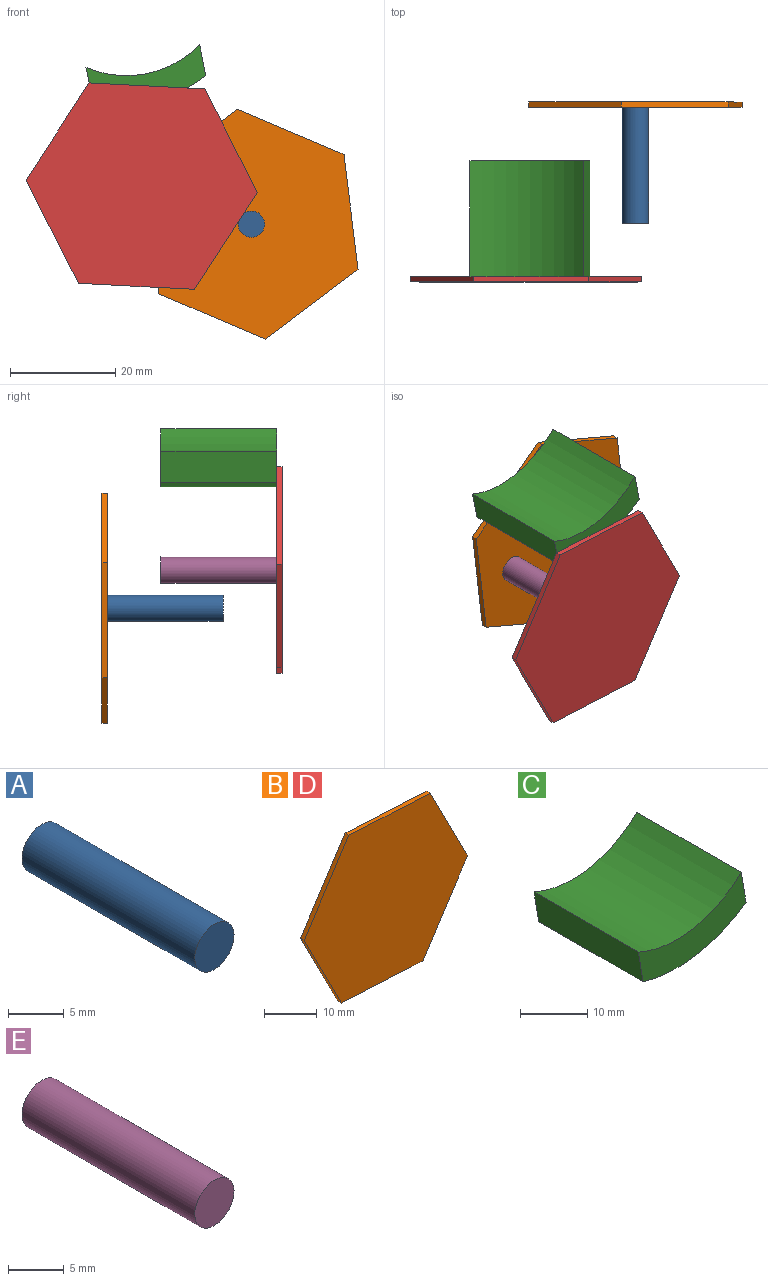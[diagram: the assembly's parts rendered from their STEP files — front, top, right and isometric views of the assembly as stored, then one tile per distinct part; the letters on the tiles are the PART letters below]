
ASSEMBLY  parts=5 mates=3
PART A: 3 faces, bbox 5x22x5 mm
  f0: cylinder r=2.5mm len=22mm, axis (0,1,0), area 345.6mm2, adj f1,f2
  f1: plane 5x5mm, normal (0,-1,0), area 19.6mm2, adj f0
  f2: plane 5x5mm, normal (0,1,0), area 19.6mm2, adj f0
PART B: 8 faces, bbox 43.9x1x39.2 mm
  f0: plane 18.46x11.98mm, normal (0.84,0,-0.54), area 22mm2, adj f1,f5,f6,f7
  f1: plane 19.6x10mm, normal (0.89,0,0.45), area 22mm2, adj f0,f2,f6,f7
  f2: plane 21.97x1.14mm, normal (0.05,0,1), area 22mm2, adj f1,f3,f6,f7
  f3: plane 18.46x11.98mm, normal (-0.84,0,0.54), area 22mm2, adj f2,f4,f6,f7
  f4: plane 19.6x10mm, normal (-0.89,0,-0.45), area 22mm2, adj f3,f5,f6,f7
  f5: plane 21.97x1.14mm, normal (-0.05,0,-1), area 22mm2, adj f0,f4,f6,f7
  f6: plane 43.94x39.2mm, normal (0,-1,0), area 1257.5mm2, adj f0,f1,f2,f3,f4,f5
  f7: plane 43.94x39.2mm, normal (0,1,0), area 1257.5mm2, adj f0,f1,f2,f3,f4,f5
PART C: 6 faces, bbox 22.7x22x10.7 mm
  f0: plane 22x5.91mm, normal (0.99,0,0.17), area 132mm2, adj f1,f3,f4,f5
  f1: cylinder r=19.46mm len=22mm, axis (0,1,0), area 514.4mm2, adj f0,f2,f4,f5
  f2: plane 22x5.91mm, normal (-0.99,0,-0.17), area 132mm2, adj f1,f3,f4,f5
  f3: cylinder r=24.64mm len=22mm, axis (0,1,0), area 501.7mm2, adj f0,f2,f4,f5
  f4: plane 22.7x10.67mm, normal (0,-1,0), area 119.5mm2, adj f0,f1,f2,f3
  f5: plane 22.7x10.67mm, normal (0,1,0), area 119.5mm2, adj f0,f1,f2,f3
PART D: same geometry as B
PART E: 3 faces, bbox 5x22x5 mm
  f0: cylinder r=2.5mm len=22mm, axis (0,1,0), area 345.6mm2, adj f1,f2
  f1: plane 5x5mm, normal (0,-1,0), area 19.6mm2, adj f0
  f2: plane 5x5mm, normal (0,1,0), area 19.6mm2, adj f0
PLACE A t=(22.66,-17.72,35.83)mm
PLACE B rot(axis=(0,-1,0),39.9deg) t=(71.69,-16.72,27.7)mm
PLACE C rot(axis=(0,-1,0),1.5deg) t=(2.53,-27.9,64.33)mm
PLACE D rot(axis=(0,1,0),180deg) t=(-80.67,-49.9,103.86)mm
PLACE E t=(21.82,-27.9,43.06)mm fixed
MATE revolute D.f7 <-> E.f0  axis (0,1,0) through (-27.42,-49.9,45.52)mm
MATE revolute C.f4 <-> D.f7  axis (0,-1,0) through (-37.42,-49.9,65.12)mm
MATE revolute B.f6 <-> A.f0  axis (0,-1,0) through (-6.58,-17.72,38.29)mm
